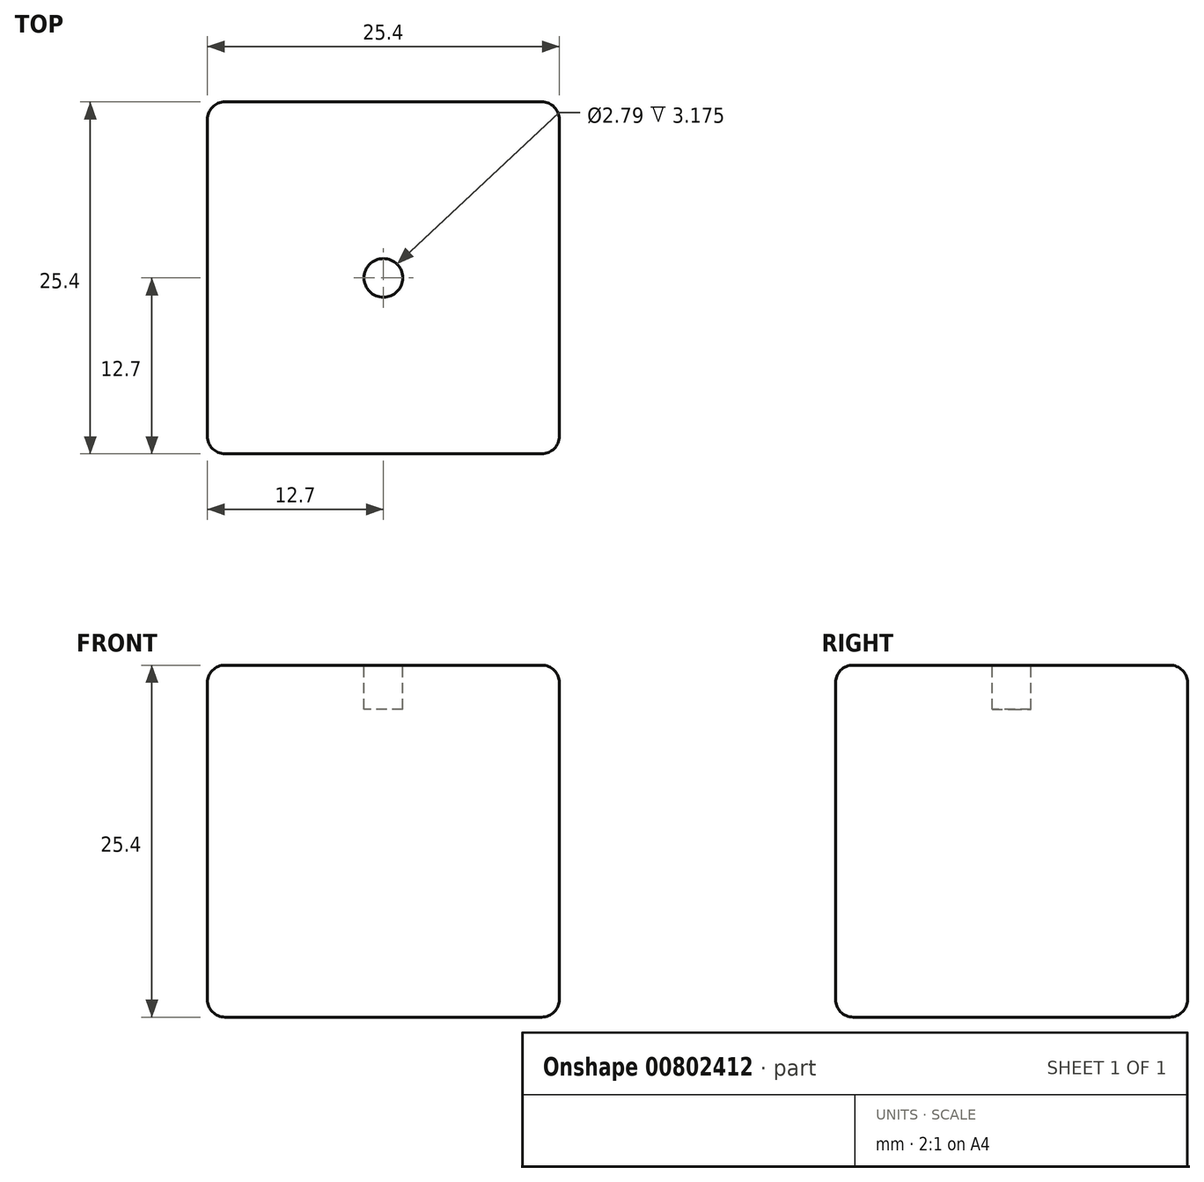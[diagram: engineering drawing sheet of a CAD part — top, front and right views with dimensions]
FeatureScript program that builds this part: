
annotation { "Feature Type Name" : "Feature", "Feature Type Description" : "" }
export const myFeature = defineFeature(function(context is Context, id is Id, definition is map)
    precondition{}
    {
        {
            var Q0;
            Q0=qCreatedBy(makeId("Front.planeOp"),FACE);
            var sketch = newSketch(context, id + "F0", { "sketchPlane" : qUnion([Q0])});
            skLineSegment(sketch, "E0.bottom", {"start": v(6.94, 14.03) * mm, "end": v(32.34, 14.03) * mm});
            skLineSegment(sketch, "E0.top", {"start": v(6.94, -11.37) * mm, "end": v(32.34, -11.37) * mm});
            skLineSegment(sketch, "E0.left", {"start": v(6.94, 14.03) * mm, "end": v(6.94, -11.37) * mm});
            skLineSegment(sketch, "E0.right", {"start": v(32.34, 14.03) * mm, "end": v(32.34, -11.37) * mm});
            skSolve(sketch);
        }
        {
            var Q0;
            Q0=makeQuery(id+"F0.imprint","IMPRINT",FACE,{"disambiguationData":[TD([[makeQuery(id+"F0.imprint","IMPRINT",EDGE,{"derivedFrom":sQuery(id+"F0.wireOp",EDGE,"E0.bottom")}),-1.0]])]});
            extrude(context, id + "F1", {"entities" : qUnion([Q0]), "depth" : 25.4 * mm, "offsetDistance" : 25.4 * mm});
        }
        {
            var Q0;
            Q0=makeQuery(id+"F1.opExtrude","SWEPT_EDGE",EDGE,{"disambiguationData":[OSD([sQuery(id+"F0.wireOp",EDGE,"E0.bottom"),sQuery(id+"F0.wireOp",EDGE,"E0.left")])]});
            var Q1;
            Q1=makeQuery(id+"F1.opExtrude","CAP_EDGE",EDGE,{"disambiguationData":[OSD([sQuery(id+"F0.wireOp",EDGE,"E0.bottom")])],"isStart":false});
            var Q2;
            Q2=makeQuery(id+"F1.opExtrude","SWEPT_FACE",FACE,{"disambiguationData":[OSD([sQuery(id+"F0.wireOp",EDGE,"E0.left")])]});
            var Q3;
            Q3=makeQuery(id+"F1.opExtrude","CAP_EDGE",EDGE,{"disambiguationData":[OSD([sQuery(id+"F0.wireOp",EDGE,"E0.top")])],"isStart":true});
            var Q4;
            Q4=makeQuery(id+"F1.opExtrude","SWEPT_FACE",FACE,{"disambiguationData":[OSD([sQuery(id+"F0.wireOp",EDGE,"E0.right")])]});
            var Q5;
            Q5=makeQuery(id+"F1.opExtrude","CAP_FACE",FACE,{"disambiguationData":[OSD([sQuery(id+"F0.wireOp",EDGE,"E0.bottom"),sQuery(id+"F0.wireOp",EDGE,"E0.top"),sQuery(id+"F0.wireOp",EDGE,"E0.left"),sQuery(id+"F0.wireOp",EDGE,"E0.right")])],"isStart":true});
            var Q6;
            Q6=makeQuery(id+"F1.opExtrude","CAP_EDGE",EDGE,{"disambiguationData":[OSD([sQuery(id+"F0.wireOp",EDGE,"E0.top")])],"isStart":false});
            fillet(context, id + "F2", {"entities" : qUnion([Q0, Q1, Q2, Q3, Q4, Q5, Q6]), "radius" : 1.27 * mm, "tangentPropagation" : true, "allowEdgeOverflow" : false});
        }
        {
            var Q0;
            Q0=makeQuery(id+"F1.opExtrude","SWEPT_FACE",FACE,{"disambiguationData":[OSD([sQuery(id+"F0.wireOp",EDGE,"E0.bottom")])]});
            var sketch = newSketch(context, id + "F3", { "sketchPlane" : qUnion([Q0])});
            skCircle(sketch, "E1", {"center": v(19.64, -12.7) * mm, "radius": 1.4 * mm});
            skLineSegment(sketch, "E2.0", {"start": v(31.07, -1.27) * mm, "end": v(8.2, -1.27) * mm, "construction": true});
            skLineSegment(sketch, "E2.1", {"start": v(8.2, -1.27) * mm, "end": v(8.2, -24.13) * mm, "construction": true});
            skLineSegment(sketch, "E2.2", {"start": v(8.2, -24.13) * mm, "end": v(31.07, -24.13) * mm, "construction": true});
            skLineSegment(sketch, "E2.3", {"start": v(31.07, -24.13) * mm, "end": v(31.07, -1.27) * mm, "construction": true});
            skLineSegment(sketch, "E3", {"start": v(19.64, -1.27) * mm, "end": v(19.64, -24.13) * mm, "construction": true});
            skLineSegment(sketch, "E4", {"start": v(8.2, -12.7) * mm, "end": v(31.07, -12.7) * mm, "construction": true});
            skSolve(sketch);
        }
        {
            var Q0;
            Q0=makeQuery(id+"F3.imprint","IMPRINT",FACE,{"disambiguationData":[TD([[makeQuery(id+"F3.imprint","IMPRINT",EDGE,{"derivedFrom":sQuery(id+"F3.wireOp",EDGE,"E1")}),1.0]])]});
            extrude(context, id + "F4", {"entities" : qUnion([Q0]), "operationType" : NewBodyOperationType.REMOVE, "oppositeDirection" : true, "depth" : 3.17 * mm, "offsetDistance" : 25.4 * mm});
        }
    });
